# Revit family: LLIFE-PRO-SM-xx
name_source: partatom
category: Lighting Fixtures
units: mm (PartAtom-declared; Revit-internal decimal feet)

## family parameters
Cut with Voids When Loaded = No
Host = Face
Light Source = Yes
Part Type = Normal
Room Calculation Point = No
Round Connector Dimension = Use Diameter
Shared = No

## types (1)
- LLIFE-PRO-SM_AUT01310080001
    Apparent Load = 3 VA
    Clevertronics_240V LED Strip = 8003081
    Clevertronics_AS2293 Classification = C0=D80 C90=D80
    Clevertronics_Annotation Size = 0 mm  [stored 0 ft]
    Clevertronics_Battery = 3.3V 5000mAh
    Clevertronics_Battery Type = Lithium Nanophosphate
    Clevertronics_Charger Method = Intelligent Current Limited Constant Voltage
    Clevertronics_Construction = Polycarbonate Enclosure
    Clevertronics_Dimensions Main Enclosure = 242mm x 125mm x 48mm
    Clevertronics_Emergency Driver = 8002924
    Clevertronics_Height = 48 mm  [stored 0.15748 ft]
    Clevertronics_IP Rating = IP20
    Clevertronics_Length = 242 mm  [stored 0.793963 ft]
    Clevertronics_MIC Number = AUT01310080001
    Clevertronics_Material = Clevertronics_Plycarbonate Base
    Clevertronics_Mounting = Surface Mounted
    Clevertronics_Operating Mode = Non-maintained
    Clevertronics_Operating Temperature = 1˚C to 40˚C
    Clevertronics_Operating Voltage = 240V AC; 50Hz
    Clevertronics_Power Consumption = 0.4 Watts (Standby), 2.7 Watts (Max)
    Clevertronics_Product Description = Lifelight Pro Emergency, Surface Mount, L10 Nanophosphate, Clevertest Plus
    Clevertronics_Replacement Battery = 1530231
    Clevertronics_Testing System = Clevertest Plus Enabled (Not activated by default)
    Clevertronics_Weight = 0.7Kg
    Clevertronics_Width = 125 mm  [stored 0.410105 ft]
    Color Filter = 16777215
    Default Elevation = 1200 mm
    Description = Lifelight Pro Emergency, Surface Mount, L10 Nanophosphate, Clevertest Plus
    Dimming Lamp Color Temperature Shift = <None>
    Lamp = Dual LED (Lifetime warranty on the lamp head and loom assembly)
    Manufacturer = Clevertronics
    Model = LLIFE-PRO-SM
    Photometric Web File = LLIFE-PRO-SM_IESA_E_ LL22440_20200331.ies
    Tilt Angle = -90.00°

note: [stored X ft] marks values corroborated as IEEE doubles in the binary element streams (Revit-internal decimal feet)

## geometry (parser evidence)
native form markers: Blend x2, Sweep x2
no freeform markers — native parametric forms only
